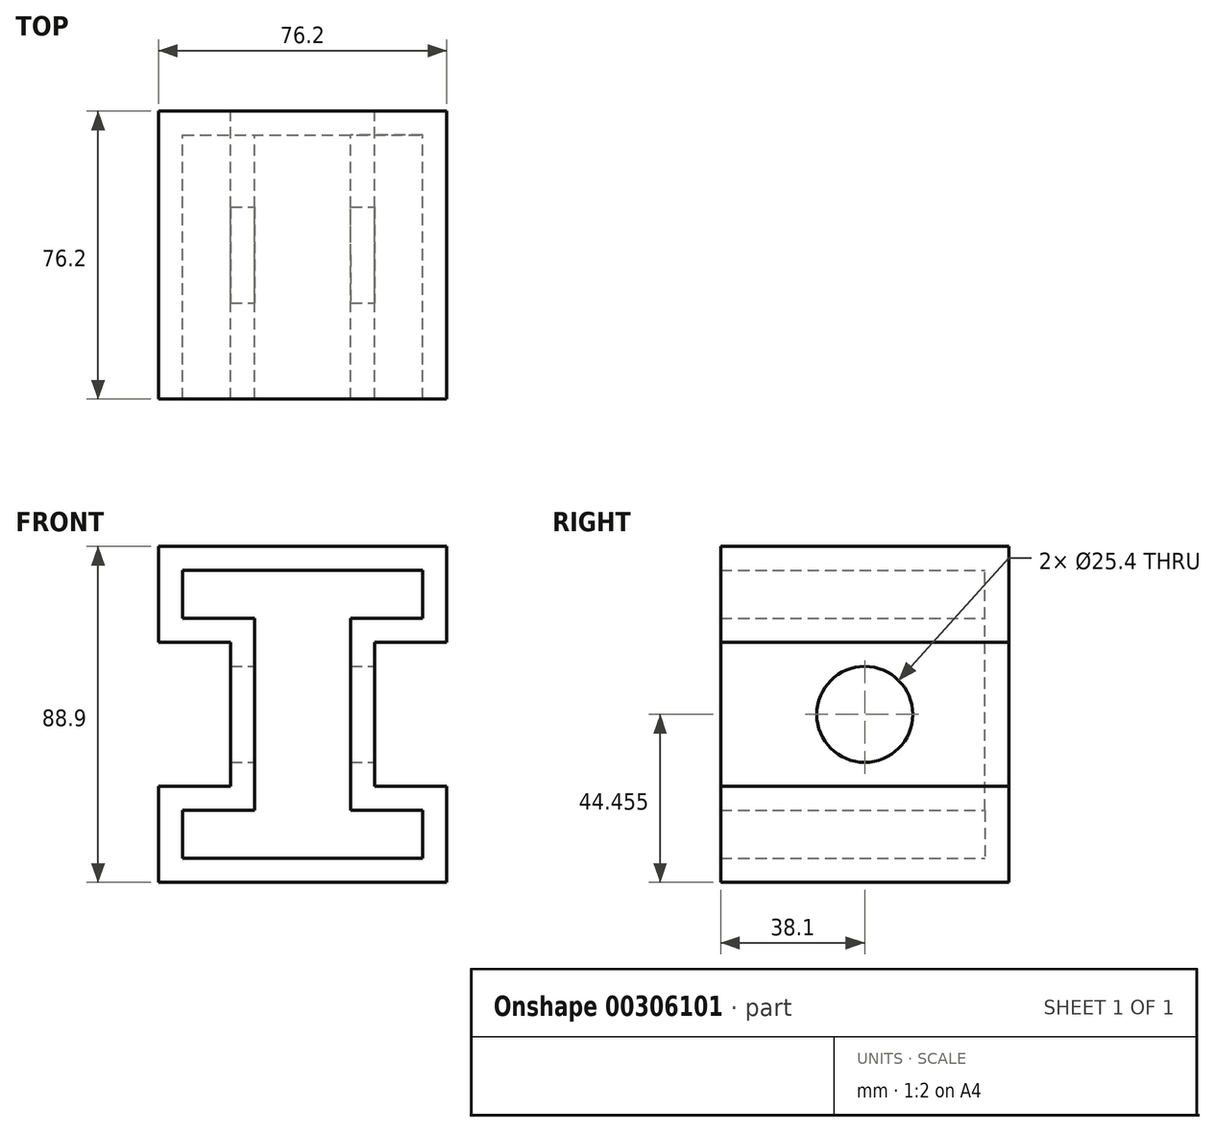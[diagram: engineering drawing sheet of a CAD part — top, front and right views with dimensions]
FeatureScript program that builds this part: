
annotation { "Feature Type Name" : "Feature", "Feature Type Description" : "" }
export const myFeature = defineFeature(function(context is Context, id is Id, definition is map)
    precondition{}
    {
        {
            var Q0;
            Q0=qCreatedBy(makeId("Front.planeOp"),FACE);
            var sketch = newSketch(context, id + "F0", { "sketchPlane" : qUnion([Q0])});
            skLineSegment(sketch, "E0", {"start": v(-38.3, -40.1) * mm, "end": v(37.9, -40.1) * mm});
            skLineSegment(sketch, "E1", {"start": v(37.9, -40.1) * mm, "end": v(37.9, -14.7) * mm});
            skLineSegment(sketch, "E2", {"start": v(37.9, -14.7) * mm, "end": v(18.85, -14.7) * mm});
            skLineSegment(sketch, "E3", {"start": v(18.85, -14.7) * mm, "end": v(18.85, 23.4) * mm});
            skLineSegment(sketch, "E4", {"start": v(18.85, 23.4) * mm, "end": v(37.9, 23.4) * mm});
            skLineSegment(sketch, "E5", {"start": v(37.9, 23.4) * mm, "end": v(37.9, 48.8) * mm});
            skLineSegment(sketch, "E6", {"start": v(37.9, 48.8) * mm, "end": v(-38.3, 48.8) * mm});
            skLineSegment(sketch, "E7", {"start": v(-38.3, 48.8) * mm, "end": v(-38.3, 23.4) * mm});
            skLineSegment(sketch, "E8", {"start": v(-38.3, 23.4) * mm, "end": v(-19.25, 23.4) * mm});
            skLineSegment(sketch, "E9", {"start": v(-19.25, 23.4) * mm, "end": v(-19.25, -14.7) * mm});
            skLineSegment(sketch, "E10", {"start": v(-19.25, -14.7) * mm, "end": v(-38.3, -14.7) * mm});
            skLineSegment(sketch, "E11", {"start": v(-38.3, -14.7) * mm, "end": v(-38.3, -40.1) * mm});
            skSolve(sketch);
        }
        {
            var Q0;
            Q0 = qSketchRegion(id + "F0", true);
            extrude(context, id + "F1", {"entities" : qUnion([Q0]), "depth" : 76.2 * mm});
        }
        {
            var Q0;
            Q0=makeQuery(id+"F1.opExtrude","CAP_FACE",FACE,{"disambiguationData":[OSD([sQuery(id+"F0.wireOp",EDGE,"E0"),sQuery(id+"F0.wireOp",EDGE,"E1"),sQuery(id+"F0.wireOp",EDGE,"E2"),sQuery(id+"F0.wireOp",EDGE,"E3"),sQuery(id+"F0.wireOp",EDGE,"E4"),sQuery(id+"F0.wireOp",EDGE,"E5"),sQuery(id+"F0.wireOp",EDGE,"E6"),sQuery(id+"F0.wireOp",EDGE,"E7"),sQuery(id+"F0.wireOp",EDGE,"E8"),sQuery(id+"F0.wireOp",EDGE,"E9"),sQuery(id+"F0.wireOp",EDGE,"E10"),sQuery(id+"F0.wireOp",EDGE,"E11")])],"isStart":false});
            shell(context, id + "F2", {"entities" : qUnion([Q0]), "thickness" : 6.35 * mm});
        }
        {
            var Q0;
            Q0=makeQuery(id+"F1.opExtrude","SWEPT_FACE",FACE,{"disambiguationData":[OSD([sQuery(id+"F0.wireOp",EDGE,"E3")])]});
            var sketch = newSketch(context, id + "F3", { "sketchPlane" : qUnion([Q0])});
            skCircle(sketch, "E12", {"center": v(-38.1, 4.34) * mm, "radius": 12.7 * mm});
            skPoint(sketch, "E12.centerSnap0", {"position": v(-38.1, 23.4) * mm});
            skPoint(sketch, "E12.centerSnap1", {"position": v(-76.2, 4.34) * mm});
            skSolve(sketch);
        }
        {
            var Q0;
            Q0 = qSketchRegion(id + "F3", true);
            extrude(context, id + "F4", {"entities" : qUnion([Q0]), "operationType" : NewBodyOperationType.REMOVE, "endBound" : BoundingType.THROUGH_ALL, "oppositeDirection" : true, "depth" : 25.4 * mm});
        }
    });
